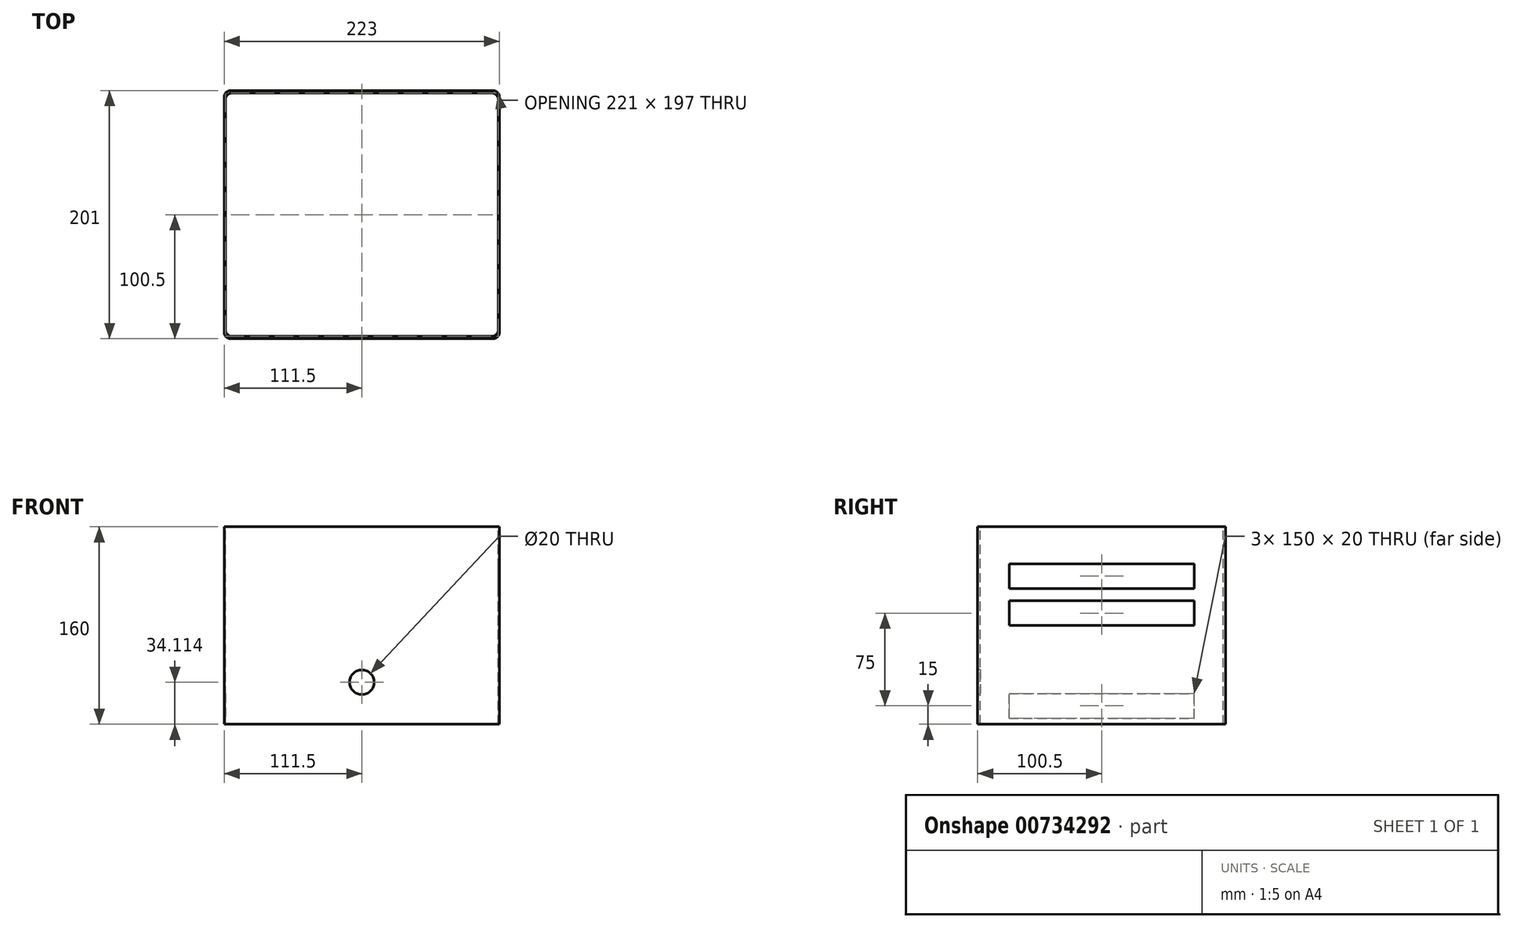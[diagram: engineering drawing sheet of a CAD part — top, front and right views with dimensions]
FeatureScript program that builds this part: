
annotation { "Feature Type Name" : "Feature", "Feature Type Description" : "" }
export const myFeature = defineFeature(function(context is Context, id is Id, definition is map)
    precondition{}
    {
        {
            var Q0;
            Q0=qCreatedBy(makeId("Top.planeOp"),FACE);
            var sketch = newSketch(context, id + "F0", { "sketchPlane" : qUnion([Q0])});
            skLineSegment(sketch, "E0.bottom", {"start": v(111.5, -100.5) * mm, "end": v(-111.5, -100.5) * mm});
            skLineSegment(sketch, "E0.top", {"start": v(111.5, 100.5) * mm, "end": v(-111.5, 100.5) * mm});
            skLineSegment(sketch, "E0.left", {"start": v(111.5, -100.5) * mm, "end": v(111.5, 100.5) * mm});
            skLineSegment(sketch, "E0.right", {"start": v(-111.5, -100.5) * mm, "end": v(-111.5, 100.5) * mm});
            skPoint(sketch, "E0.middle", {"position": v(0, 0) * mm});
            skSolve(sketch);
        }
        {
            var Q0;
            Q0 = qSketchRegion(id + "F0", true);
            extrude(context, id + "F1", {"entities" : qUnion([Q0]), "depth" : 160 * mm, "offsetDistance" : 25 * mm});
        }
        {
            var Q0;
            Q0=makeQuery(id+"F1.opExtrude","CAP_FACE",FACE,{"disambiguationData":[OSD([sQuery(id+"F0.wireOp",EDGE,"E0.bottom"),sQuery(id+"F0.wireOp",EDGE,"E0.top"),sQuery(id+"F0.wireOp",EDGE,"E0.left"),sQuery(id+"F0.wireOp",EDGE,"E0.right")])],"isStart":false});
            var sketch = newSketch(context, id + "F2", { "sketchPlane" : qUnion([Q0])});
            skLineSegment(sketch, "E1.bottom", {"start": v(110.5, -98.5) * mm, "end": v(-110.5, -98.5) * mm});
            skLineSegment(sketch, "E1.top", {"start": v(110.5, 98.5) * mm, "end": v(-110.5, 98.5) * mm});
            skLineSegment(sketch, "E1.left", {"start": v(110.5, -98.5) * mm, "end": v(110.5, 98.5) * mm});
            skLineSegment(sketch, "E1.right", {"start": v(-110.5, -98.5) * mm, "end": v(-110.5, 98.5) * mm});
            skPoint(sketch, "E1.middle", {"position": v(0, 0) * mm});
            skSolve(sketch);
        }
        {
            var Q0;
            Q0 = qSketchRegion(id + "F2", true);
            extrude(context, id + "F3", {"entities" : qUnion([Q0]), "operationType" : NewBodyOperationType.REMOVE, "oppositeDirection" : true, "depth" : 160 * mm, "offsetDistance" : 25 * mm});
        }
        {
            var Q0;
            Q0=makeQuery(id+"F1.opExtrude","SWEPT_FACE",FACE,{"disambiguationData":[OSD([sQuery(id+"F0.wireOp",EDGE,"E0.left")])]});
            var sketch = newSketch(context, id + "F4", { "sketchPlane" : qUnion([Q0])});
            skLineSegment(sketch, "E2.bottom", {"start": v(75, 110) * mm, "end": v(-75, 110) * mm});
            skLineSegment(sketch, "E2.top", {"start": v(75, 130) * mm, "end": v(-75, 130) * mm});
            skLineSegment(sketch, "E2.left", {"start": v(75, 110) * mm, "end": v(75, 130) * mm});
            skLineSegment(sketch, "E2.right", {"start": v(-75, 110) * mm, "end": v(-75, 130) * mm});
            skPoint(sketch, "E2.middle", {"position": v(0, 120) * mm});
            skLineSegment(sketch, "E3.bottom", {"start": v(75, 80) * mm, "end": v(-75, 80) * mm});
            skLineSegment(sketch, "E3.top", {"start": v(75, 100) * mm, "end": v(-75, 100) * mm});
            skLineSegment(sketch, "E3.left", {"start": v(75, 80) * mm, "end": v(75, 100) * mm});
            skLineSegment(sketch, "E3.right", {"start": v(-75, 80) * mm, "end": v(-75, 100) * mm});
            skPoint(sketch, "E3.middle", {"position": v(0, 90) * mm});
            skSolve(sketch);
        }
        {
            var Q0;
            Q0 = qSketchRegion(id + "F4", true);
            extrude(context, id + "F5", {"entities" : qUnion([Q0]), "operationType" : NewBodyOperationType.REMOVE, "oppositeDirection" : true, "depth" : 25 * mm, "offsetDistance" : 25 * mm});
        }
        {
            var Q0;
            Q0=makeQuery(id+"F1.opExtrude","SWEPT_FACE",FACE,{"disambiguationData":[OSD([sQuery(id+"F0.wireOp",EDGE,"E0.right")])]});
            var sketch = newSketch(context, id + "F6", { "sketchPlane" : qUnion([Q0])});
            skLineSegment(sketch, "E4.bottom", {"start": v(75, 5) * mm, "end": v(-75, 5) * mm});
            skLineSegment(sketch, "E4.top", {"start": v(75, 25) * mm, "end": v(-75, 25) * mm});
            skLineSegment(sketch, "E4.left", {"start": v(75, 5) * mm, "end": v(75, 25) * mm});
            skLineSegment(sketch, "E4.right", {"start": v(-75, 5) * mm, "end": v(-75, 25) * mm});
            skPoint(sketch, "E4.middle", {"position": v(0, 15) * mm});
            skSolve(sketch);
        }
        {
            var Q0;
            Q0 = qSketchRegion(id + "F6", true);
            extrude(context, id + "F7", {"entities" : qUnion([Q0]), "operationType" : NewBodyOperationType.REMOVE, "oppositeDirection" : true, "depth" : 25 * mm, "offsetDistance" : 25 * mm});
        }
        {
            var Q0;
            Q0=makeQuery(id+"F1.opExtrude","SWEPT_FACE",FACE,{"disambiguationData":[OSD([sQuery(id+"F0.wireOp",EDGE,"E0.bottom")])]});
            var sketch = newSketch(context, id + "F8", { "sketchPlane" : qUnion([Q0])});
            skCircle(sketch, "E5", {"center": v(0, 34.11) * mm, "radius": 10 * mm});
            skSolve(sketch);
        }
        {
            var Q0;
            Q0 = qSketchRegion(id + "F8", true);
            extrude(context, id + "F9", {"entities" : qUnion([Q0]), "operationType" : NewBodyOperationType.REMOVE, "oppositeDirection" : true, "depth" : 25 * mm, "offsetDistance" : 25 * mm});
        }
        {
            var Q0;
            Q0=makeQuery(id+"F3.boolean.opBoolean","COPY",EDGE,{"derivedFrom":makeQuery(id+"F3.opExtrude","SWEPT_EDGE",EDGE,{"disambiguationData":[OSD([sQuery(id+"F2.wireOp",EDGE,"E1.bottom"),sQuery(id+"F2.wireOp",EDGE,"E1.right")])]})});
            var Q1;
            Q1=makeQuery(id+"F1.opExtrude","SWEPT_EDGE",EDGE,{"disambiguationData":[OSD([sQuery(id+"F0.wireOp",EDGE,"E0.bottom"),sQuery(id+"F0.wireOp",EDGE,"E0.right")])]});
            var Q2;
            Q2=makeQuery(id+"F1.opExtrude","SWEPT_EDGE",EDGE,{"disambiguationData":[OSD([sQuery(id+"F0.wireOp",EDGE,"E0.top"),sQuery(id+"F0.wireOp",EDGE,"E0.right")])]});
            var Q3;
            Q3=makeQuery(id+"F3.boolean.opBoolean","COPY",EDGE,{"derivedFrom":makeQuery(id+"F3.opExtrude","SWEPT_EDGE",EDGE,{"disambiguationData":[OSD([sQuery(id+"F2.wireOp",EDGE,"E1.top"),sQuery(id+"F2.wireOp",EDGE,"E1.right")])]})});
            var Q4;
            Q4=makeQuery(id+"F3.boolean.opBoolean","COPY",EDGE,{"derivedFrom":makeQuery(id+"F3.opExtrude","SWEPT_EDGE",EDGE,{"disambiguationData":[OSD([sQuery(id+"F2.wireOp",EDGE,"E1.top"),sQuery(id+"F2.wireOp",EDGE,"E1.left")])]})});
            var Q5;
            Q5=makeQuery(id+"F3.boolean.opBoolean","COPY",EDGE,{"derivedFrom":makeQuery(id+"F3.opExtrude","SWEPT_EDGE",EDGE,{"disambiguationData":[OSD([sQuery(id+"F2.wireOp",EDGE,"E1.bottom"),sQuery(id+"F2.wireOp",EDGE,"E1.left")])]})});
            var Q6;
            Q6=makeQuery(id+"F1.opExtrude","SWEPT_EDGE",EDGE,{"disambiguationData":[OSD([sQuery(id+"F0.wireOp",EDGE,"E0.top"),sQuery(id+"F0.wireOp",EDGE,"E0.left")])]});
            var Q7;
            Q7=makeQuery(id+"F1.opExtrude","SWEPT_EDGE",EDGE,{"disambiguationData":[OSD([sQuery(id+"F0.wireOp",EDGE,"E0.bottom"),sQuery(id+"F0.wireOp",EDGE,"E0.left")])]});
            fillet(context, id + "F10", {"entities" : qUnion([Q0, Q1, Q2, Q3, Q4, Q5, Q6, Q7]), "radius" : 5 * mm, "tangentPropagation" : true, "allowEdgeOverflow" : false});
        }
    });
